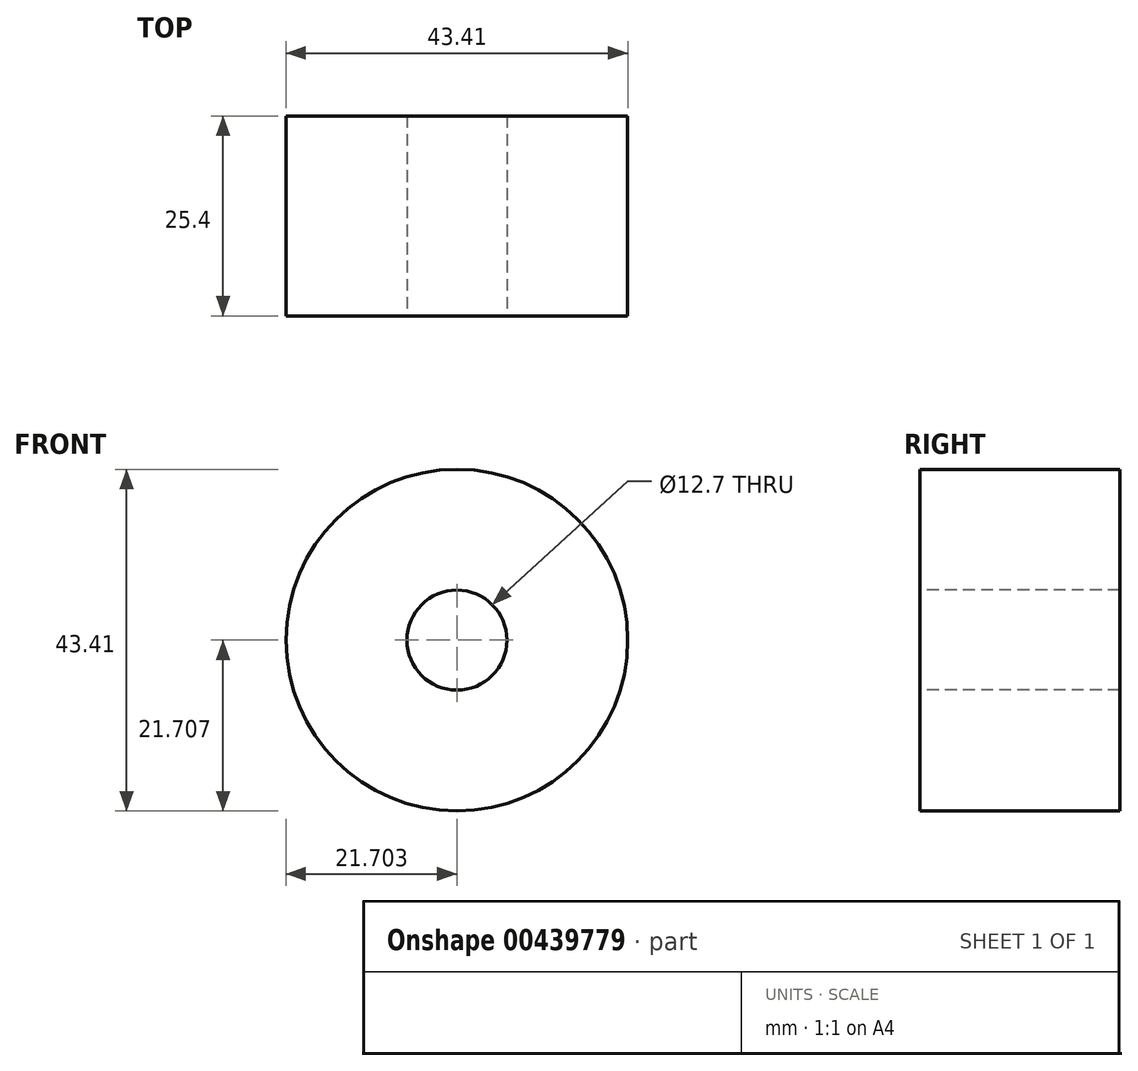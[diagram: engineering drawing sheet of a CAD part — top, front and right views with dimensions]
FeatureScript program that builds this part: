
annotation { "Feature Type Name" : "Feature", "Feature Type Description" : "" }
export const myFeature = defineFeature(function(context is Context, id is Id, definition is map)
    precondition{}
    {
        {
            var Q0;
            Q0=qCreatedBy(makeId("Front.planeOp"),FACE);
            var sketch = newSketch(context, id + "F0", { "sketchPlane" : qUnion([Q0])});
            skCircle(sketch, "E0", {"center": v(-47.39, 39.09) * mm, "radius": 21.7 * mm});
            skSolve(sketch);
        }
        {
            var Q0;
            Q0=makeQuery(id+"F0.imprint","IMPRINT",FACE,{"disambiguationData":[TD([[makeQuery(id+"F0.imprint","IMPRINT",EDGE,{"derivedFrom":sQuery(id+"F0.wireOp",EDGE,"E0")}),1.0]])]});
            extrude(context, id + "F1", {"entities" : qUnion([Q0]), "depth" : 25.4 * mm});
        }
        {
            var Q0;
            Q0=makeQuery(id+"F1.opExtrude","CAP_FACE",FACE,{"disambiguationData":[OSD([sQuery(id+"F0.wireOp",EDGE,"E0")])],"isStart":false});
            var sketch = newSketch(context, id + "F2", { "sketchPlane" : qUnion([Q0])});
            skCircle(sketch, "E1", {"center": v(-47.39, 39.09) * mm, "radius": 10.07 * mm});
            skSolve(sketch);
        }
        {
            var Q0;
            Q0=sQuery(id+"F2.wireOp",VERTEX,"E1.center");
            var Q1;
            Q1=makeQuery(id+"F1.opExtrude","SWEPT_BODY",BODY,{"disambiguationData":[OSD([sQuery(id+"F0.wireOp",EDGE,"E0")])]});
            hole(context, id + "F3", {"style" : HoleStyle.SIMPLE, "endStyle" : HoleEndStyle.THROUGH, "holeDiameter" : 12.7 * mm, "isTappedThrough" : true, "tappedDepth" : 12.7 * mm, "tapClearance" : 3, "startFromSketch" : true, "locations" : qUnion([Q0]), "scope" : qUnion([Q1])});
        }
    });
